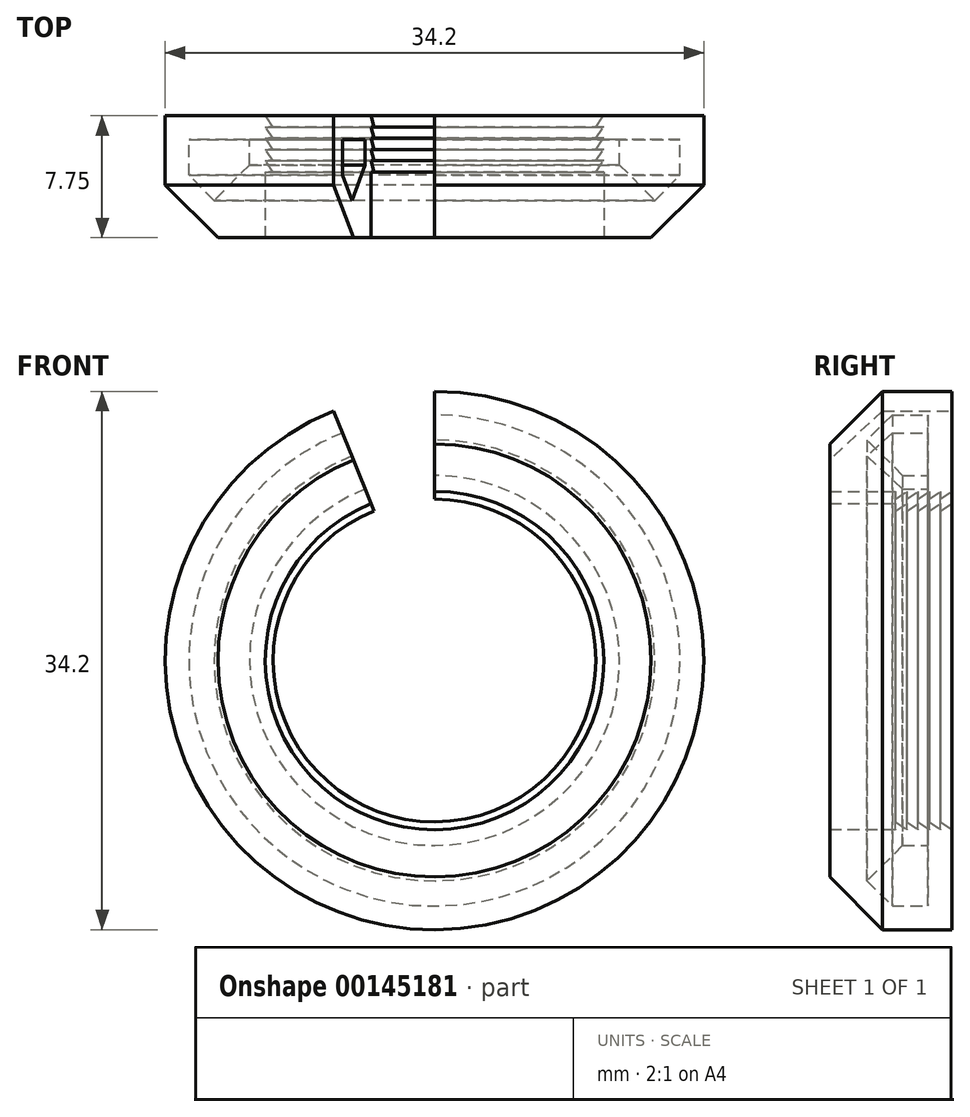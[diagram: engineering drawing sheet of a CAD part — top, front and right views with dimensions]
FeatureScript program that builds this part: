
annotation { "Feature Type Name" : "Feature", "Feature Type Description" : "" }
export const myFeature = defineFeature(function(context is Context, id is Id, definition is map)
    precondition{}
    {
        {
            var Q0;
            Q0=qCreatedBy(makeId("Top.planeOp"),FACE);
            var sketch = newSketch(context, id + "F0", { "sketchPlane" : qUnion([Q0])});
            skLineSegment(sketch, "E0", {"start": v(0, -58.44) * mm, "end": v(0, 42) * mm, "construction": true});
            skSolve(sketch);
        }
        {
            var Q0;
            Q0=qCreatedBy(makeId("Right.planeOp"),FACE);
            var sketch = newSketch(context, id + "F1", { "sketchPlane" : qUnion([Q0])});
            skLineSegment(sketch, "E1", {"start": v(-13.88, 10.75) * mm, "end": v(-13.88, 20.5) * mm});
            skLineSegment(sketch, "E2", {"start": v(-13.88, 20.5) * mm, "end": v(-14.88, 20.5) * mm});
            skLineSegment(sketch, "E3", {"start": v(-14.88, 20.5) * mm, "end": v(-21.63, 13.75) * mm});
            skLineSegment(sketch, "E4", {"start": v(-21.63, 13.75) * mm, "end": v(-21.63, 10.75) * mm});
            skLineSegment(sketch, "E5", {"start": v(-21.63, 10.75) * mm, "end": v(-17.45, 10.75) * mm});
            skLineSegment(sketch, "E6", {"start": v(-17.45, 10.75) * mm, "end": v(-17.45, 10.25) * mm});
            skLineSegment(sketch, "E7", {"start": v(-17.45, 10.25) * mm, "end": v(-16.73, 10.75) * mm});
            skLineSegment(sketch, "E8", {"start": v(-16.73, 10.75) * mm, "end": v(-16.73, 10.25) * mm});
            skLineSegment(sketch, "E9", {"start": v(-16.73, 10.25) * mm, "end": v(-16.02, 10.75) * mm});
            skLineSegment(sketch, "E10", {"start": v(-16.02, 10.75) * mm, "end": v(-16.02, 10.25) * mm});
            skLineSegment(sketch, "E11", {"start": v(-16.02, 10.25) * mm, "end": v(-15.3, 10.75) * mm});
            skLineSegment(sketch, "E12", {"start": v(-15.3, 10.75) * mm, "end": v(-15.3, 10.25) * mm});
            skLineSegment(sketch, "E13", {"start": v(-15.3, 10.25) * mm, "end": v(-14.6, 10.75) * mm});
            skLineSegment(sketch, "E14", {"start": v(-14.6, 10.75) * mm, "end": v(-14.6, 10.25) * mm});
            skLineSegment(sketch, "E15", {"start": v(-14.6, 10.25) * mm, "end": v(-13.88, 10.75) * mm});
            skSolve(sketch);
        }
        {
            var Q0;
            Q0 = qSketchRegion(id + "F1", true);
            var Q1;
            Q1=sQuery(id+"F0.wireOp",EDGE,"E0");
            revolve(context, id + "F2", {"entities" : qUnion([Q0]), "axis" : qUnion([Q1]), "revolveType" : RevolveType.ONE_DIRECTION, "angle" : 338 * degree});
        }
        {
            var Q0;
            Q0=qCreatedBy(makeId("Front.planeOp"),FACE);
            var sketch = newSketch(context, id + "F3", { "sketchPlane" : qUnion([Q0])});
            skCircle(sketch, "E16", {"center": v(0, 0) * mm, "radius": 17.1 * mm});
            skCircle(sketch, "E17", {"center": v(0, 0) * mm, "radius": 29.1 * mm});
            skSolve(sketch);
        }
        {
            var Q0;
            Q0 = qSketchRegion(id + "F3", true);
            extrude(context, id + "F4", {"entities" : qUnion([Q0]), "operationType" : NewBodyOperationType.REMOVE, "depth" : 25 * mm});
        }
        {
            var Q0;
            Q0=makeQuery(id+"F2.opRevolve","CAP_FACE",FACE,{"disambiguationData":[OSD([sQuery(id+"F1.wireOp",EDGE,"E1"),sQuery(id+"F1.wireOp",EDGE,"E2"),sQuery(id+"F1.wireOp",EDGE,"E3"),sQuery(id+"F1.wireOp",EDGE,"E4"),sQuery(id+"F1.wireOp",EDGE,"E5"),sQuery(id+"F1.wireOp",EDGE,"E6"),sQuery(id+"F1.wireOp",EDGE,"E7"),sQuery(id+"F1.wireOp",EDGE,"E8"),sQuery(id+"F1.wireOp",EDGE,"E9"),sQuery(id+"F1.wireOp",EDGE,"E10"),sQuery(id+"F1.wireOp",EDGE,"E11"),sQuery(id+"F1.wireOp",EDGE,"E12"),sQuery(id+"F1.wireOp",EDGE,"E13"),sQuery(id+"F1.wireOp",EDGE,"E14"),sQuery(id+"F1.wireOp",EDGE,"E15")])],"isStart":false});
            var sketch = newSketch(context, id + "F5", { "sketchPlane" : qUnion([Q0])});
            skLineSegment(sketch, "E18", {"start": v(-15.38, 15.6) * mm, "end": v(-17.66, 15.6) * mm});
            skLineSegment(sketch, "E19", {"start": v(-17.66, 15.6) * mm, "end": v(-19.25, 14) * mm});
            skLineSegment(sketch, "E20", {"start": v(-15.38, 11.75) * mm, "end": v(-15.38, 15.6) * mm});
            skLineSegment(sketch, "E21", {"start": v(-19.25, 14) * mm, "end": v(-17, 11.75) * mm});
            skLineSegment(sketch, "E22", {"start": v(-17, 11.75) * mm, "end": v(-15.38, 11.75) * mm});
            skSolve(sketch);
        }
        {
            var Q0;
            Q0 = qSketchRegion(id + "F5", true);
            var Q1;
            Q1=sQuery(id+"F0.wireOp",EDGE,"E0");
            revolve(context, id + "F6", {"operationType" : NewBodyOperationType.REMOVE, "entities" : qUnion([Q0]), "axis" : qUnion([Q1]), "revolveType" : RevolveType.FULL, "oppositeDirection" : true});
        }
    });
